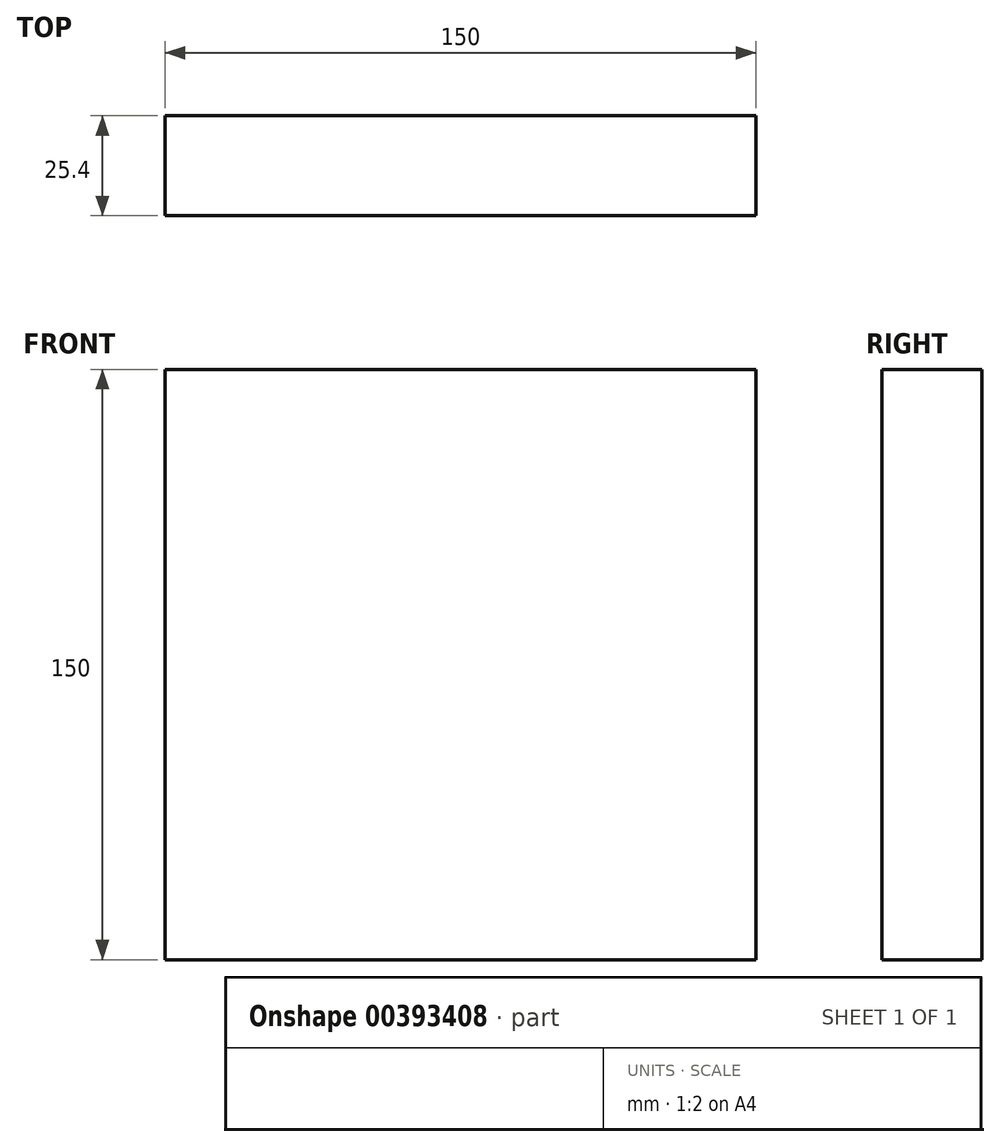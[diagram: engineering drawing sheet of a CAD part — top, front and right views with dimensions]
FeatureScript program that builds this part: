
annotation { "Feature Type Name" : "Feature", "Feature Type Description" : "" }
export const myFeature = defineFeature(function(context is Context, id is Id, definition is map)
    precondition{}
    {
        {
            var Q0;
            Q0=qCreatedBy(makeId("Front.planeOp"),FACE);
            var sketch = newSketch(context, id + "F0", { "sketchPlane" : qUnion([Q0])});
            skLineSegment(sketch, "E0.bottom", {"start": v(75, -75) * mm, "end": v(-75, -75) * mm});
            skLineSegment(sketch, "E0.top", {"start": v(75, 75) * mm, "end": v(-75, 75) * mm});
            skLineSegment(sketch, "E0.left", {"start": v(75, -75) * mm, "end": v(75, 75) * mm});
            skLineSegment(sketch, "E0.right", {"start": v(-75, -75) * mm, "end": v(-75, 75) * mm});
            skPoint(sketch, "E0.middle", {"position": v(0, 0) * mm});
            skSolve(sketch);
        }
        {
            var Q0;
            Q0 = qSketchRegion(id + "F0", true);
            extrude(context, id + "F1", {"entities" : qUnion([Q0]), "depth" : 25.4 * mm});
        }
    });
